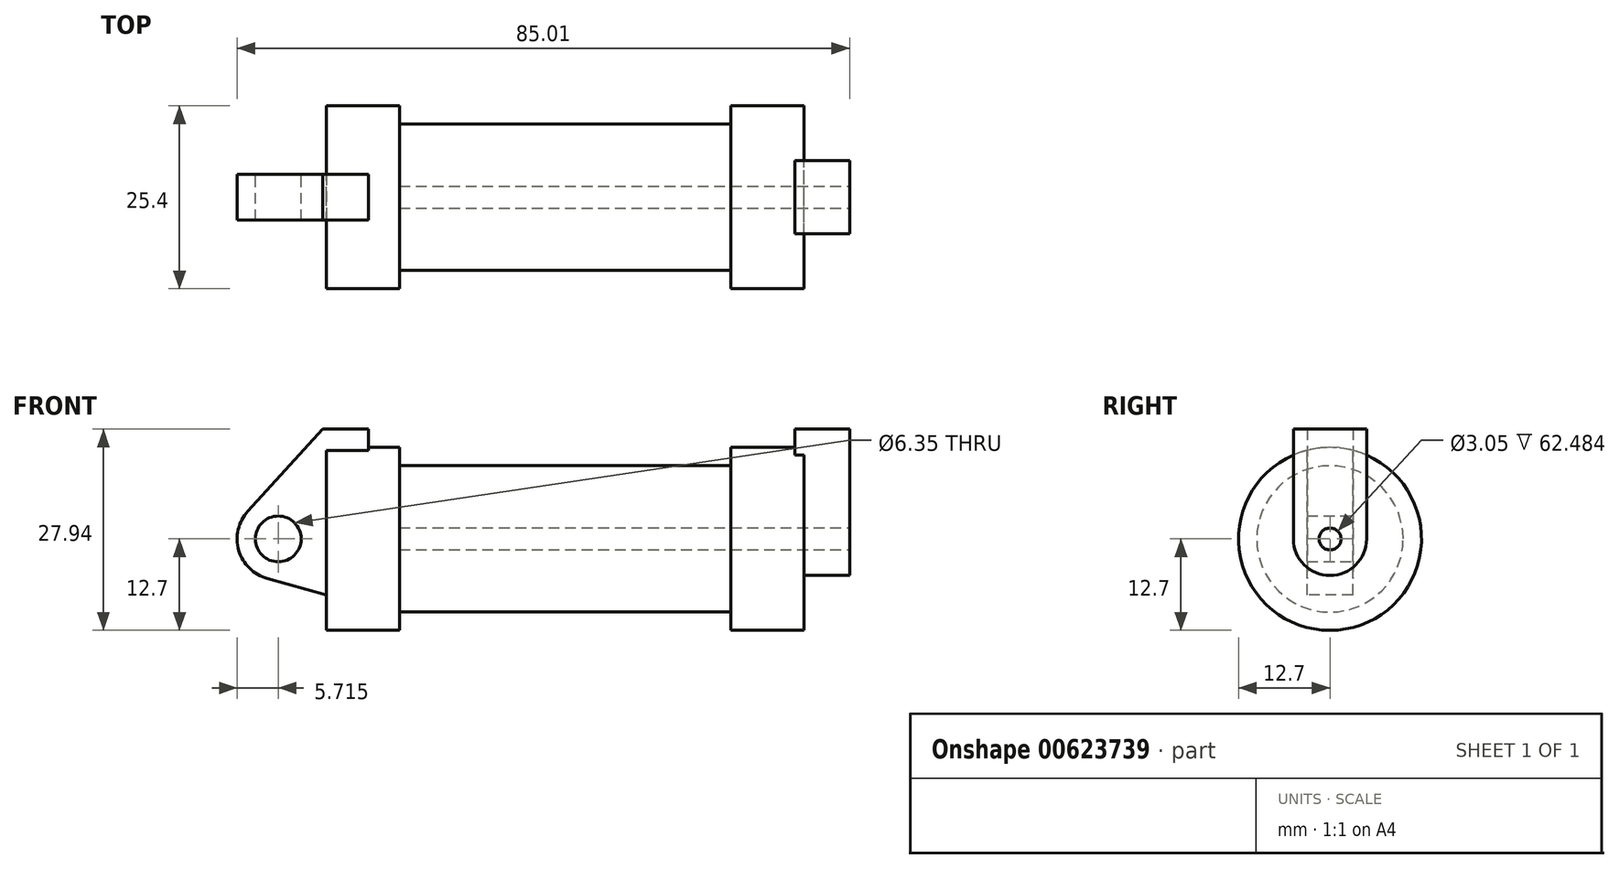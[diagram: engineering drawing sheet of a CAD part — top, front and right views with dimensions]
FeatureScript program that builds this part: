
annotation { "Feature Type Name" : "Feature", "Feature Type Description" : "" }
export const myFeature = defineFeature(function(context is Context, id is Id, definition is map)
    precondition{}
    {
        {
            var Q0;
            Q0=qCreatedBy(makeId("Front.planeOp"),FACE);
            var sketch = newSketch(context, id + "F0", { "sketchPlane" : qUnion([Q0])});
            skLineSegment(sketch, "E0", {"start": v(0, 0) * mm, "end": v(0, 12.7) * mm});
            skLineSegment(sketch, "E1", {"start": v(0, 12.7) * mm, "end": v(10.16, 12.7) * mm});
            skLineSegment(sketch, "E2", {"start": v(10.16, 12.7) * mm, "end": v(10.16, 10.16) * mm});
            skLineSegment(sketch, "E3", {"start": v(10.16, 10.16) * mm, "end": v(56.13, 10.16) * mm});
            skLineSegment(sketch, "E4", {"start": v(56.13, 10.16) * mm, "end": v(56.13, 12.7) * mm});
            skLineSegment(sketch, "E5", {"start": v(56.13, 12.7) * mm, "end": v(66.3, 12.7) * mm});
            skLineSegment(sketch, "E6", {"start": v(66.3, 12.7) * mm, "end": v(66.3, 0) * mm});
            skLineSegment(sketch, "E7", {"start": v(66.3, 0) * mm, "end": v(0, 0) * mm});
            skLineSegment(sketch, "E8", {"start": v(5.84, 15.24) * mm, "end": v(-0.5, 15.24) * mm});
            skLineSegment(sketch, "E9", {"start": v(-0.5, 15.24) * mm, "end": v(-10.88, 3.85) * mm});
            skLineSegment(sketch, "E10", {"start": v(0, 0) * mm, "end": v(-6.65, 0) * mm});
            skCircle(sketch, "E11", {"center": v(-6.65, 0) * mm, "radius": 5.72 * mm});
            skCircle(sketch, "E12", {"center": v(-6.65, 0) * mm, "radius": 3.18 * mm});
            skLineSegment(sketch, "E13", {"start": v(5.84, 15.24) * mm, "end": v(5.84, -9.4) * mm});
            skLineSegment(sketch, "E14", {"start": v(5.84, -9.4) * mm, "end": v(-8.18, -5.5) * mm});
            skSolve(sketch);
        }
        {
            var Q0;
            {var subQ1=sQuery(id+"F0.wireOp",EDGE,"E0");Q0=makeQuery(id+"F0.imprint","IMPRINT",FACE,{"disambiguationData":[TD([[makeQuery(id+"F0.imprint","IMPRINT",EDGE,{"derivedFrom":subQ1}),1.0]])]});}
            var Q1;
            {var subQ0=sQuery(id+"F0.wireOp",EDGE,"E0");Q1=makeQuery(id+"F0.imprint","IMPRINT",FACE,{"disambiguationData":[TD([[makeQuery(id+"F0.imprint","IMPRINT",EDGE,{"derivedFrom":subQ0}),-1.0]])]});}
            var Q2;
            {var subQ5=sQuery(id+"F0.wireOp",EDGE,"E12");Q2=makeQuery(id+"F0.imprint","IMPRINT",FACE,{"disambiguationData":[TD([[makeQuery(id+"F0.imprint","IMPRINT",EDGE,{"derivedFrom":subQ5}),-1.0]])]});}
            var Q3;
            {var subQ0=sQuery(id+"F0.wireOp",EDGE,"E14");Q3=makeQuery(id+"F0.imprint","IMPRINT",FACE,{"disambiguationData":[TD([[makeQuery(id+"F0.imprint","IMPRINT",EDGE,{"derivedFrom":subQ0}),-1.0]])]});}
            extrude(context, id + "F1", {"entities" : qUnion([Q0, Q1, Q2, Q3]), "depth" : 6.35 * mm, "offsetDistance" : 25.4 * mm, "symmetric" : true});
        }
        {
            var Q0;
            {var subQ0=sQuery(id+"F0.wireOp",EDGE,"E2");Q0=makeQuery(id+"F0.imprint","IMPRINT",FACE,{"disambiguationData":[TD([[makeQuery(id+"F0.imprint","IMPRINT",EDGE,{"derivedFrom":subQ0}),-1.0]])]});}
            var Q1;
            {var subQ0=sQuery(id+"F0.wireOp",EDGE,"E0");Q1=makeQuery(id+"F0.imprint","IMPRINT",FACE,{"disambiguationData":[TD([[makeQuery(id+"F0.imprint","IMPRINT",EDGE,{"derivedFrom":subQ0}),-1.0]])]});}
            var Q2;
            Q2=sQuery(id+"F0.wireOp",EDGE,"E7");
            revolve(context, id + "F2", {"operationType" : NewBodyOperationType.ADD, "entities" : qUnion([Q0, Q1]), "axis" : qUnion([Q2]), "revolveType" : RevolveType.FULL});
        }
        {
            var Q0;
            Q0=makeQuery(id+"F2.opRevolve","SWEPT_FACE",FACE,{"disambiguationData":[OSD([sQuery(id+"F0.wireOp",EDGE,"E6")])]});
            var sketch = newSketch(context, id + "F3", { "sketchPlane" : qUnion([Q0])});
            skCircle(sketch, "E15", {"center": v(0, 0) * mm, "radius": 1.52 * mm});
            skCircle(sketch, "E16", {"center": v(0, 0) * mm, "radius": 5.08 * mm});
            skLineSegment(sketch, "E17", {"start": v(5.08, 0) * mm, "end": v(5.08, 15.24) * mm});
            skLineSegment(sketch, "E18", {"start": v(-5.08, 0) * mm, "end": v(-5.08, 15.24) * mm});
            skLineSegment(sketch, "E19", {"start": v(-5.08, 15.24) * mm, "end": v(5.08, 15.24) * mm});
            skSolve(sketch);
        }
        {
            var Q0;
            {var subQ0=sQuery(id+"F3.wireOp",EDGE,"E19");Q0=makeQuery(id+"F3.imprint","IMPRINT",FACE,{"disambiguationData":[TD([[makeQuery(id+"F3.imprint","IMPRINT",EDGE,{"derivedFrom":subQ0}),-1.0]])]});}
            extrude(context, id + "F4", {"entities" : qUnion([Q0]), "operationType" : NewBodyOperationType.ADD, "oppositeDirection" : true, "depth" : 1.27 * mm, "offsetDistance" : 25.4 * mm});
        }
        {
            var Q0;
            Q0=makeQuery(id+"F3.imprint","IMPRINT",FACE,{"disambiguationData":[TD([[makeQuery(id+"F3.imprint","IMPRINT",EDGE,{"derivedFrom":sQuery(id+"F3.wireOp",EDGE,"E15")}),1.0]])]});
            var Q1;
            Q1=makeQuery(id+"F2.opRevolve","SWEPT_FACE",FACE,{"disambiguationData":[OSD([sQuery(id+"F0.wireOp",EDGE,"E2")])]});
            extrude(context, id + "F5", {"entities" : qUnion([Q0]), "operationType" : NewBodyOperationType.REMOVE, "endBound" : BoundingType.UP_TO_SURFACE, "oppositeDirection" : true, "depth" : 25.4 * mm, "endBoundEntityFace" : qUnion([Q1]), "offsetDistance" : 25.4 * mm});
        }
        {
            var Q0;
            Q0=makeQuery(id+"F3.imprint","IMPRINT",FACE,{"disambiguationData":[TD([[makeQuery(id+"F3.imprint","IMPRINT",EDGE,{"derivedFrom":sQuery(id+"F3.wireOp",EDGE,"E15")}),-1.0]])]});
            var Q1;
            {var subQ0=sQuery(id+"F3.wireOp",EDGE,"E17");var subQ1=sQuery(id+"F3.wireOp",EDGE,"E16");var subQ2=makeQuery(id+"F3.imprint","INTERSECT",VERTEX,{"derivedFrom":[subQ1,subQ0]});Q1=makeQuery(id+"F3.imprint","IMPRINT",FACE,{"disambiguationData":[TD([[makeQuery(id+"F3.imprint","IMPRINT",EDGE,{"disambiguationData":[TD([[subQ2,-1.0]])],"derivedFrom":subQ1}),-1.0]])]});}
            var Q2;
            {var subQ0=sQuery(id+"F3.wireOp",EDGE,"E19");Q2=makeQuery(id+"F3.imprint","IMPRINT",FACE,{"disambiguationData":[TD([[makeQuery(id+"F3.imprint","IMPRINT",EDGE,{"derivedFrom":subQ0}),-1.0]])]});}
            extrude(context, id + "F6", {"entities" : qUnion([Q0, Q1, Q2]), "operationType" : NewBodyOperationType.ADD, "depth" : 6.35 * mm, "offsetDistance" : 25.4 * mm});
        }
    });
